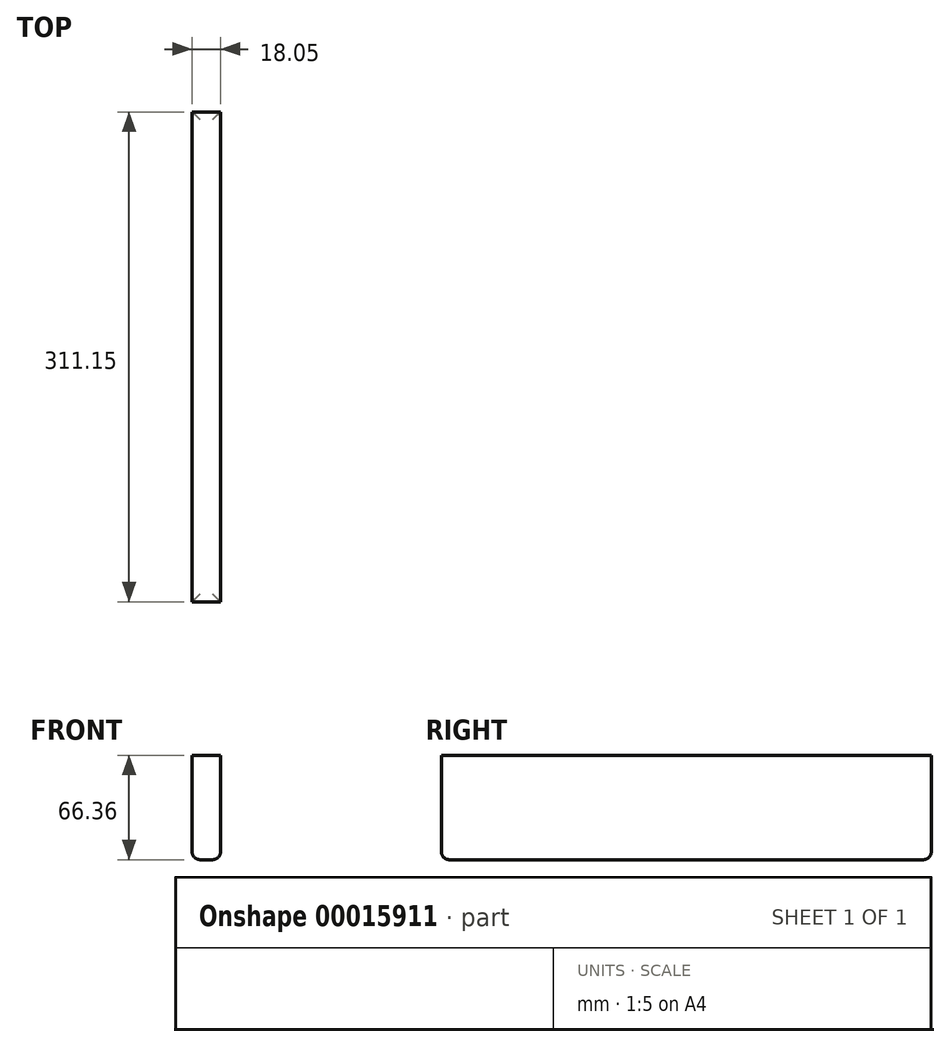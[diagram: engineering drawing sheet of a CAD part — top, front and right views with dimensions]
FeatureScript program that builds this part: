
annotation { "Feature Type Name" : "Feature", "Feature Type Description" : "" }
export const myFeature = defineFeature(function(context is Context, id is Id, definition is map)
    precondition{}
    {
        {
            var Q0;
            Q0=qCreatedBy(makeId("Front.planeOp"),FACE);
            var sketch = newSketch(context, id + "F0", { "sketchPlane" : qUnion([Q0])});
            skLineSegment(sketch, "E0.bottom", {"start": v(-13.17, 33.67) * mm, "end": v(4.88, 33.67) * mm});
            skLineSegment(sketch, "E0.top", {"start": v(-13.17, -32.7) * mm, "end": v(4.88, -32.7) * mm});
            skLineSegment(sketch, "E0.left", {"start": v(-13.17, 33.67) * mm, "end": v(-13.17, -32.7) * mm});
            skLineSegment(sketch, "E0.right", {"start": v(4.88, 33.67) * mm, "end": v(4.88, -32.7) * mm});
            skSolve(sketch);
        }
        {
            var Q0;
            Q0=makeQuery(id+"F0.imprint","IMPRINT",FACE,{"disambiguationData":[TD([[makeQuery(id+"F0.imprint","IMPRINT",EDGE,{"derivedFrom":sQuery(id+"F0.wireOp",EDGE,"E0.bottom")}),-1.0]])]});
            extrude(context, id + "F1", {"entities" : qUnion([Q0]), "depth" : 311.15 * mm});
        }
        {
            var Q0;
            Q0=makeQuery(id+"F1.opExtrude","SWEPT_FACE",FACE,{"disambiguationData":[OSD([sQuery(id+"F0.wireOp",EDGE,"E0.top")])]});
            fillet(context, id + "F2", {"entities" : qUnion([Q0]), "radius" : 5 * mm, "tangentPropagation" : true, "allowEdgeOverflow" : false});
        }
    });
